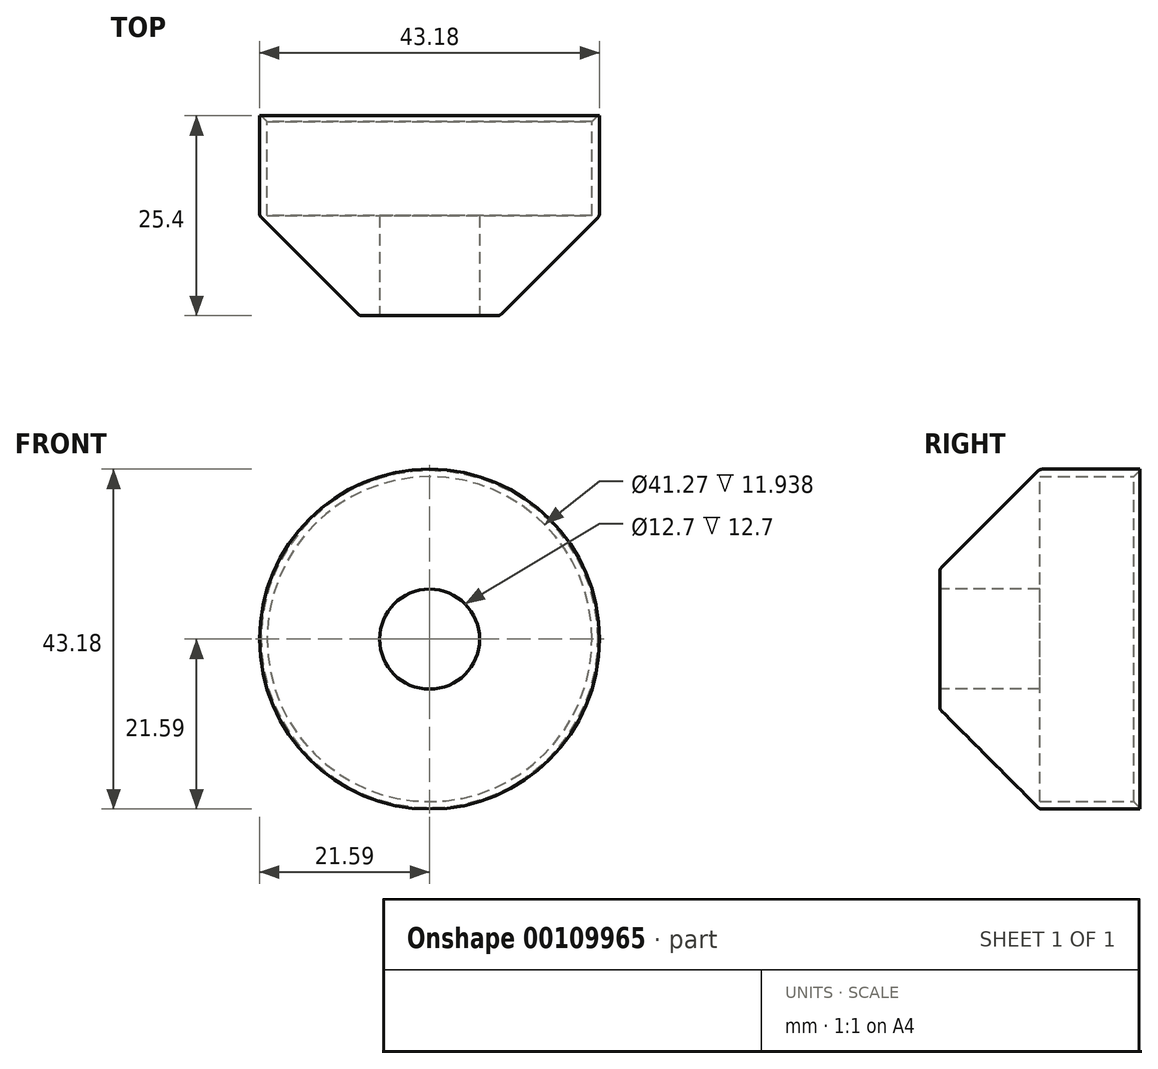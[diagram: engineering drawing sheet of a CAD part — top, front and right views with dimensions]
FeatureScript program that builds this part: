
annotation { "Feature Type Name" : "Feature", "Feature Type Description" : "" }
export const myFeature = defineFeature(function(context is Context, id is Id, definition is map)
    precondition{}
    {
        {
            var Q0;
            Q0=qCreatedBy(makeId("Front.planeOp"),FACE);
            var sketch = newSketch(context, id + "F0", { "sketchPlane" : qUnion([Q0])});
            skCircle(sketch, "E0", {"center": v(0, 0) * mm, "radius": 21.59 * mm});
            skCircle(sketch, "E1", {"center": v(0, 0) * mm, "radius": 20.64 * mm});
            skSolve(sketch);
        }
        {
            var Q0;
            Q0=makeQuery(id+"F0.imprint","IMPRINT",FACE,{"disambiguationData":[TD([[makeQuery(id+"F0.imprint","IMPRINT",EDGE,{"derivedFrom":sQuery(id+"F0.wireOp",EDGE,"E0")}),1.0]])]});
            extrude(context, id + "F1", {"entities" : qUnion([Q0]), "depth" : 12.7 * mm});
        }
        {
            var Q0;
            Q0=makeQuery(id+"F1.opExtrude","CAP_FACE",FACE,{"disambiguationData":[OSD([sQuery(id+"F0.wireOp",EDGE,"E0"),sQuery(id+"F0.wireOp",EDGE,"E1")])],"isStart":false});
            var sketch = newSketch(context, id + "F2", { "sketchPlane" : qUnion([Q0])});
            skCircle(sketch, "E2.0", {"center": v(0, 0) * mm, "radius": 21.59 * mm});
            skSolve(sketch);
        }
        {
            var Q0;
            Q0 = qSketchRegion(id + "F2", true);
            extrude(context, id + "F3", {"entities" : qUnion([Q0]), "operationType" : NewBodyOperationType.ADD, "depth" : 12.7 * mm, "hasDraft" : true, "draftAngle" : 45 * degree, "draftPullDirection" : true});
        }
        {
            var Q0;
            Q0=makeQuery(id+"F3.boolean.opBoolean","MERGE",EDGE,{"derivedFrom":[makeQuery(id+"F1.opExtrude","CAP_EDGE",EDGE,{"disambiguationData":[OSD([sQuery(id+"F0.wireOp",EDGE,"E0")])],"isStart":false}),makeQuery(id+"F3.opExtrude","CAP_EDGE",EDGE,{"disambiguationData":[OSD([sQuery(id+"F2.wireOp",EDGE,"E2.0")])],"isStart":true})]});
            var Q1;
            Q1=makeQuery(id+"F3.opExtrude","CAP_EDGE",EDGE,{"disambiguationData":[OSD([sQuery(id+"F2.wireOp",EDGE,"E2.0")])],"isStart":false});
            fillet(context, id + "F4", {"entities" : qUnion([Q0, Q1]), "radius" : 0.76 * mm, "tangentPropagation" : true, "allowEdgeOverflow" : false});
        }
        {
            var Q0;
            Q0=makeQuery(id+"F3.opExtrude","CAP_FACE",FACE,{"disambiguationData":[OSD([sQuery(id+"F2.wireOp",EDGE,"E2.0")])],"isStart":false});
            var sketch = newSketch(context, id + "F5", { "sketchPlane" : qUnion([Q0])});
            skCircle(sketch, "E3", {"center": v(0, 0) * mm, "radius": 6.35 * mm});
            skSolve(sketch);
        }
        {
            var Q0;
            Q0=makeQuery(id+"F5.imprint","IMPRINT",FACE,{"disambiguationData":[TD([[makeQuery(id+"F5.imprint","IMPRINT",EDGE,{"derivedFrom":sQuery(id+"F5.wireOp",EDGE,"E3")}),1.0]])]});
            extrude(context, id + "F6", {"entities" : qUnion([Q0]), "operationType" : NewBodyOperationType.REMOVE, "oppositeDirection" : true, "depth" : 25.4 * mm});
        }
        {
            var Q0;
            Q0=makeQuery(id+"F6.boolean.opBoolean","COPY",EDGE,{"derivedFrom":makeQuery(id+"F6.opExtrude","CAP_EDGE",EDGE,{"disambiguationData":[OSD([sQuery(id+"F5.wireOp",EDGE,"E3")])],"isStart":true})});
            var Q1;
            Q1=makeQuery(id+"F1.opExtrude","CAP_EDGE",EDGE,{"disambiguationData":[OSD([sQuery(id+"F0.wireOp",EDGE,"E1")])],"isStart":true});
            chamfer(context, id + "F7", {"entities" : qUnion([Q0, Q1]), "width" : 0.76 * mm, "tangentPropagation" : true});
        }
    });
